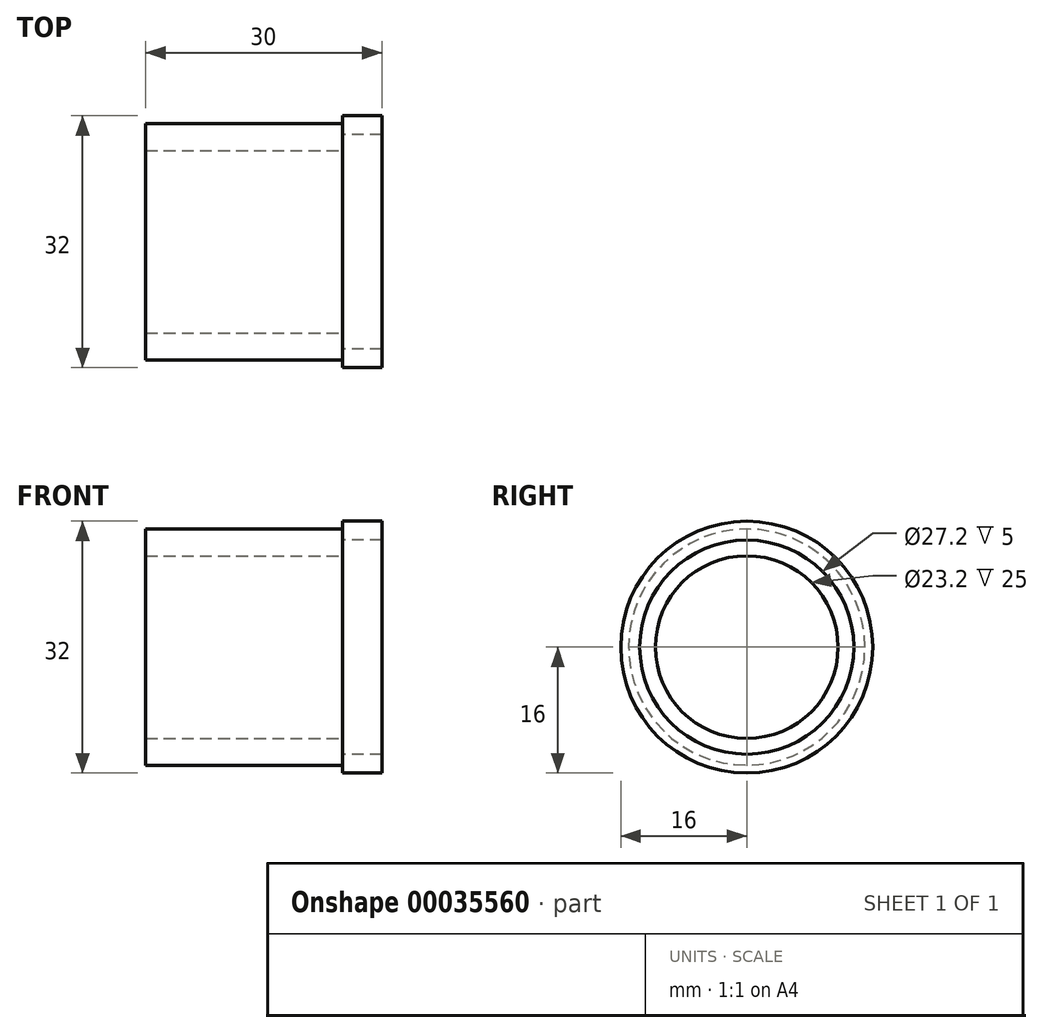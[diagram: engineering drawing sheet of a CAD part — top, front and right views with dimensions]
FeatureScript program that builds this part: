
annotation { "Feature Type Name" : "Feature", "Feature Type Description" : "" }
export const myFeature = defineFeature(function(context is Context, id is Id, definition is map)
    precondition{}
    {
        {
            var Q0;
            Q0=qCreatedBy(makeId("Right.planeOp"),FACE);
            var sketch = newSketch(context, id + "F0", { "sketchPlane" : qUnion([Q0])});
            skCircle(sketch, "E0", {"center": v(0, 0) * mm, "radius": 13.6 * mm});
            skCircle(sketch, "E1", {"center": v(0, 0) * mm, "radius": 16 * mm});
            skSolve(sketch);
        }
        {
            var Q0;
            Q0=makeQuery(id+"F0.imprint","IMPRINT",FACE,{"disambiguationData":[TD([[makeQuery(id+"F0.imprint","IMPRINT",EDGE,{"derivedFrom":sQuery(id+"F0.wireOp",EDGE,"E0")}),-1.0]])]});
            extrude(context, id + "F1", {"entities" : qUnion([Q0]), "depth" : 5 * mm});
        }
        {
            var Q0;
            Q0=makeQuery(id+"F1.opExtrude","CAP_FACE",FACE,{"disambiguationData":[OSD([sQuery(id+"F0.wireOp",EDGE,"E0"),sQuery(id+"F0.wireOp",EDGE,"E1")])],"isStart":true});
            var sketch = newSketch(context, id + "F2", { "sketchPlane" : qUnion([Q0])});
            skCircle(sketch, "E2", {"center": v(0, 0) * mm, "radius": 15 * mm});
            skCircle(sketch, "E3", {"center": v(0, 0) * mm, "radius": 11.6 * mm});
            skSolve(sketch);
        }
        {
            var Q0;
            Q0 = qSketchRegion(id + "F2", true);
            extrude(context, id + "F3", {"entities" : qUnion([Q0]), "operationType" : NewBodyOperationType.ADD, "depth" : 25 * mm});
        }
    });
